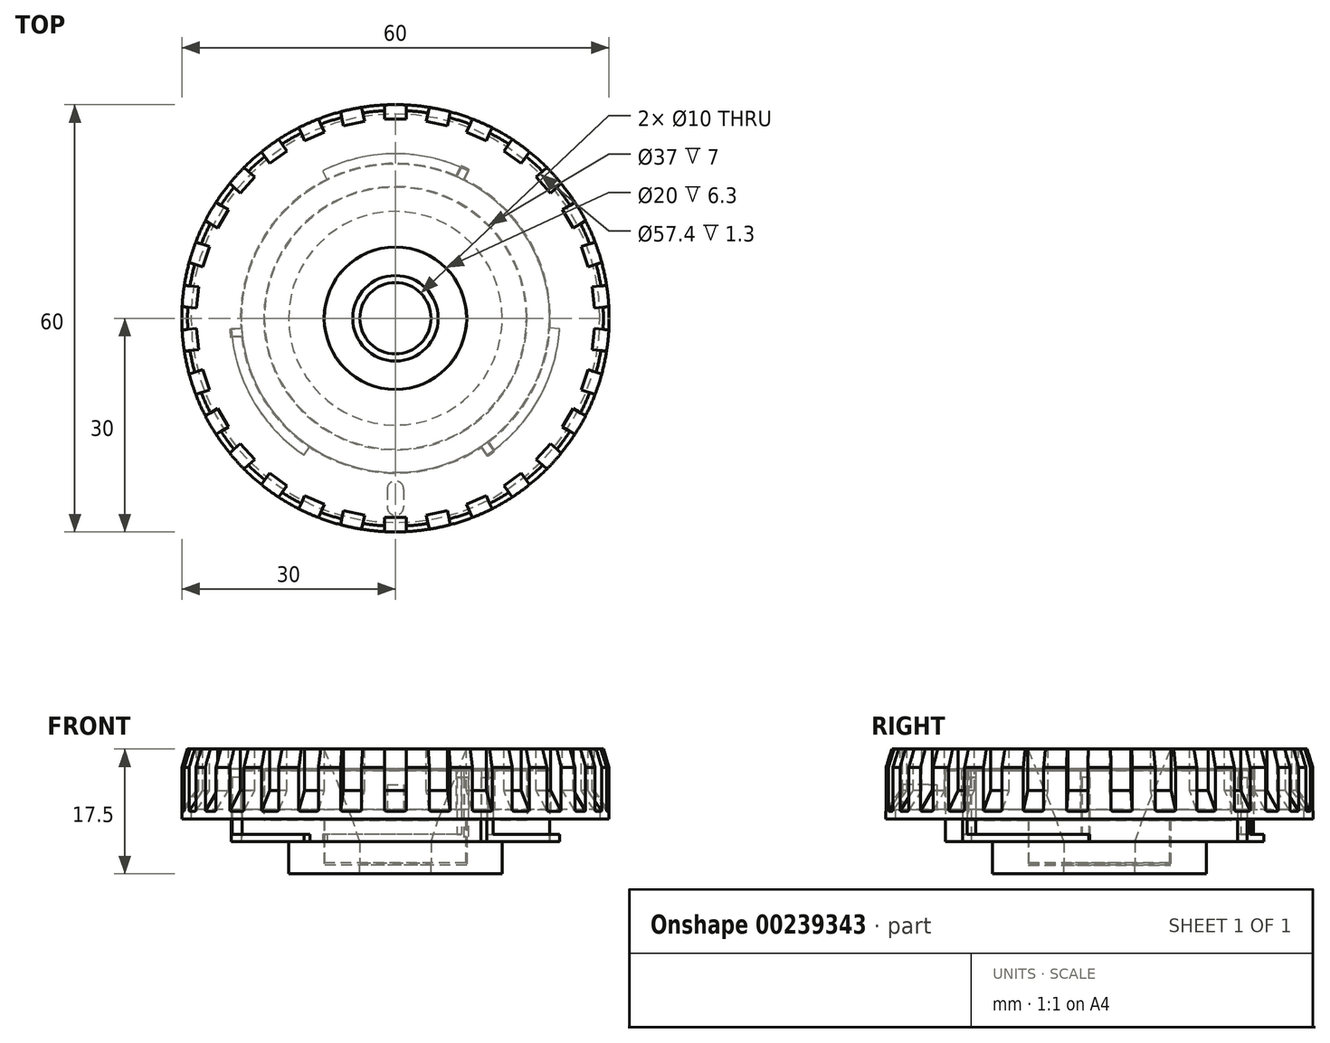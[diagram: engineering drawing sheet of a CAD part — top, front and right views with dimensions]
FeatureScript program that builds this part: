
annotation { "Feature Type Name" : "Feature", "Feature Type Description" : "" }
export const myFeature = defineFeature(function(context is Context, id is Id, definition is map)
    precondition{}
    {
        {
            var Q0;
            Q0=qCreatedBy(makeId("Top.planeOp"),FACE);
            var sketch = newSketch(context, id + "F0", { "sketchPlane" : qUnion([Q0])});
            skCircle(sketch, "E0", {"center": v(0, 0) * mm, "radius": 21.65 * mm});
            skCircle(sketch, "E1", {"center": v(0, 0) * mm, "radius": 18.5 * mm});
            skArc(sketch, "E2", {"start": v(-23.05, -1.47) * mm, "mid": v(-20, -11.55) * mm, "end": v(-12.8, -19.23) * mm});
            skLineSegment(sketch, "E3", {"start": v(0, 0) * mm, "end": v(10.25, 20.7) * mm, "construction": true});
            skLineSegment(sketch, "E4", {"start": v(0, 0) * mm, "end": v(-10.25, 20.7) * mm, "construction": true});
            skLineSegment(sketch, "E5", {"start": v(10.25, 20.7) * mm, "end": v(0, 23.1) * mm, "construction": true});
            skLineSegment(sketch, "E6", {"start": v(0, 23.1) * mm, "end": v(-10.25, 20.7) * mm, "construction": true});
            skLineSegment(sketch, "E7", {"start": v(0, 0) * mm, "end": v(-20, -11.55) * mm, "construction": true});
            skLineSegment(sketch, "E8", {"start": v(0, 0) * mm, "end": v(-23.05, -1.47) * mm, "construction": true});
            skLineSegment(sketch, "E9", {"start": v(0, 0) * mm, "end": v(-12.8, -19.23) * mm, "construction": true});
            skLineSegment(sketch, "E10", {"start": v(0, 0) * mm, "end": v(20, -11.55) * mm, "construction": true});
            skLineSegment(sketch, "E11", {"start": v(0, 0) * mm, "end": v(23.05, -1.47) * mm, "construction": true});
            skLineSegment(sketch, "E12", {"start": v(0, 0) * mm, "end": v(12.8, -19.23) * mm, "construction": true});
            skLineSegment(sketch, "E13", {"start": v(-23.05, -1.47) * mm, "end": v(-12.8, -19.23) * mm, "construction": true});
            skLineSegment(sketch, "E14", {"start": v(23.05, -1.47) * mm, "end": v(12.8, -19.23) * mm, "construction": true});
            skLineSegment(sketch, "E15", {"start": v(-23.05, -1.47) * mm, "end": v(-20, -11.55) * mm, "construction": true});
            skLineSegment(sketch, "E16", {"start": v(-12.8, -19.23) * mm, "end": v(-20, -11.55) * mm, "construction": true});
            skLineSegment(sketch, "E17", {"start": v(12.8, -19.23) * mm, "end": v(20, -11.55) * mm, "construction": true});
            skLineSegment(sketch, "E18", {"start": v(23.05, -1.47) * mm, "end": v(20, -11.55) * mm, "construction": true});
            skLineSegment(sketch, "E19", {"start": v(-10.25, 20.7) * mm, "end": v(-9.6, 19.4) * mm});
            skLineSegment(sketch, "E20", {"start": v(10.25, 20.7) * mm, "end": v(9.6, 19.4) * mm});
            skLineSegment(sketch, "E21", {"start": v(23.05, -1.47) * mm, "end": v(21.6, -1.38) * mm});
            skLineSegment(sketch, "E22", {"start": v(12.8, -19.23) * mm, "end": v(12, -18.02) * mm});
            skLineSegment(sketch, "E23", {"start": v(-23.05, -1.47) * mm, "end": v(-21.6, -1.38) * mm});
            skLineSegment(sketch, "E24", {"start": v(-12.8, -19.23) * mm, "end": v(-12, -18.02) * mm});
            skArc(sketch, "E25.trimOffspring", {"start": v(10.25, 20.7) * mm, "mid": v(0, 23.1) * mm, "end": v(-10.25, 20.7) * mm});
            skArc(sketch, "E26.trimOffspring", {"start": v(12.8, -19.23) * mm, "mid": v(20, -11.55) * mm, "end": v(23.05, -1.47) * mm});
            skCircle(sketch, "E27", {"center": v(0, 0) * mm, "radius": 10 * mm});
            skLineSegment(sketch, "E28", {"start": v(8.6, 19.86) * mm, "end": v(9.25, 21.17) * mm});
            skLineSegment(sketch, "E29", {"start": v(12.9, -17.39) * mm, "end": v(13.7, -18.6) * mm});
            skLineSegment(sketch, "E30", {"start": v(-21.5, -2.48) * mm, "end": v(-22.96, -2.57) * mm});
            skSolve(sketch);
        }
        {
            var Q0;
            Q0=makeQuery(id+"F0.imprint","IMPRINT",FACE,{"disambiguationData":[TD([[makeQuery(id+"F0.imprint","IMPRINT",EDGE,{"derivedFrom":sQuery(id+"F0.wireOp",EDGE,"E1")}),-1.0]])]});
            extrude(context, id + "F1", {"entities" : qUnion([Q0]), "depth" : 10 * mm});
        }
        {
            var Q0;
            Q0=makeQuery(id+"F0.imprint","IMPRINT",FACE,{"disambiguationData":[TD([[makeQuery(id+"F0.imprint","IMPRINT",EDGE,{"derivedFrom":sQuery(id+"F0.wireOp",EDGE,"E1")}),1.0]])]});
            extrude(context, id + "F2", {"entities" : qUnion([Q0]), "operationType" : NewBodyOperationType.ADD, "depth" : 3 * mm});
        }
        {
            var Q0;
            {var subQ0=sQuery(id+"F0.wireOp",EDGE,"E24");Q0=makeQuery(id+"F0.imprint","IMPRINT",FACE,{"disambiguationData":[TD([[makeQuery(id+"F0.imprint","IMPRINT",EDGE,{"derivedFrom":subQ0}),1.0]])]});}
            var Q1;
            {var subQ0=sQuery(id+"F0.wireOp",EDGE,"E21");Q1=makeQuery(id+"F0.imprint","IMPRINT",FACE,{"disambiguationData":[TD([[makeQuery(id+"F0.imprint","IMPRINT",EDGE,{"derivedFrom":subQ0}),1.0]])]});}
            var Q2;
            {var subQ0=sQuery(id+"F0.wireOp",EDGE,"E19");Q2=makeQuery(id+"F0.imprint","IMPRINT",FACE,{"disambiguationData":[TD([[makeQuery(id+"F0.imprint","IMPRINT",EDGE,{"derivedFrom":subQ0}),1.0]])]});}
            extrude(context, id + "F3", {"entities" : qUnion([Q0, Q1, Q2]), "operationType" : NewBodyOperationType.ADD, "depth" : 1 * mm});
        }
        {
            var Q0;
            {var subQ0=sQuery(id+"F0.wireOp",EDGE,"E22");Q0=makeQuery(id+"F0.imprint","IMPRINT",FACE,{"disambiguationData":[TD([[makeQuery(id+"F0.imprint","IMPRINT",EDGE,{"derivedFrom":subQ0}),-1.0]])]});}
            var Q1;
            {var subQ0=sQuery(id+"F0.wireOp",EDGE,"E23");Q1=makeQuery(id+"F0.imprint","IMPRINT",FACE,{"disambiguationData":[TD([[makeQuery(id+"F0.imprint","IMPRINT",EDGE,{"derivedFrom":subQ0}),-1.0]])]});}
            var Q2;
            {var subQ0=sQuery(id+"F0.wireOp",EDGE,"E20");Q2=makeQuery(id+"F0.imprint","IMPRINT",FACE,{"disambiguationData":[TD([[makeQuery(id+"F0.imprint","IMPRINT",EDGE,{"derivedFrom":subQ0}),-1.0]])]});}
            extrude(context, id + "F4", {"entities" : qUnion([Q0, Q1, Q2]), "operationType" : NewBodyOperationType.ADD, "depth" : 9 * mm});
        }
        {
            var Q0;
            Q0=qCreatedBy(makeId("Top.planeOp"),FACE);
            var sketch = newSketch(context, id + "F5", { "sketchPlane" : qUnion([Q0])});
            skCircle(sketch, "E31", {"center": v(0, 0) * mm, "radius": 21.75 * mm});
            skCircle(sketch, "E32", {"center": v(0, 0) * mm, "radius": 18.4 * mm});
            skArc(sketch, "E33", {"start": v(-23.25, -1.53) * mm, "mid": v(-23.2, -2.13) * mm, "end": v(-23.14, -2.72) * mm});
            skLineSegment(sketch, "E34", {"start": v(0, 0) * mm, "end": v(10.3, 20.9) * mm, "construction": true});
            skLineSegment(sketch, "E35", {"start": v(0, 0) * mm, "end": v(-9.61, 19.5) * mm, "construction": true});
            skLineSegment(sketch, "E36", {"start": v(10.3, 20.9) * mm, "end": v(0, 23.3) * mm, "construction": true});
            skLineSegment(sketch, "E37", {"start": v(0, 23.3) * mm, "end": v(-10.3, 20.9) * mm, "construction": true});
            skLineSegment(sketch, "E38", {"start": v(0, 0) * mm, "end": v(-20.18, -11.65) * mm, "construction": true});
            skLineSegment(sketch, "E39", {"start": v(0, 0) * mm, "end": v(-23.25, -1.53) * mm, "construction": true});
            skLineSegment(sketch, "E40", {"start": v(0, 0) * mm, "end": v(-12.09, -18.08) * mm, "construction": true});
            skLineSegment(sketch, "E41", {"start": v(0, 0) * mm, "end": v(20.18, -11.65) * mm, "construction": true});
            skLineSegment(sketch, "E42", {"start": v(0, 0) * mm, "end": v(21.7, -1.43) * mm, "construction": true});
            skLineSegment(sketch, "E43", {"start": v(0, 0) * mm, "end": v(12.95, -19.37) * mm, "construction": true});
            skLineSegment(sketch, "E44", {"start": v(-23.25, -1.53) * mm, "end": v(-12.95, -19.37) * mm, "construction": true});
            skLineSegment(sketch, "E45", {"start": v(23.25, -1.53) * mm, "end": v(12.95, -19.37) * mm, "construction": true});
            skLineSegment(sketch, "E46", {"start": v(-23.25, -1.53) * mm, "end": v(-20.18, -11.65) * mm, "construction": true});
            skLineSegment(sketch, "E47", {"start": v(-12.95, -19.37) * mm, "end": v(-20.18, -11.65) * mm, "construction": true});
            skLineSegment(sketch, "E48", {"start": v(12.95, -19.37) * mm, "end": v(20.18, -11.65) * mm, "construction": true});
            skLineSegment(sketch, "E49", {"start": v(23.25, -1.53) * mm, "end": v(20.18, -11.65) * mm, "construction": true});
            skLineSegment(sketch, "E50", {"start": v(10.3, 20.9) * mm, "end": v(9.61, 19.5) * mm});
            skLineSegment(sketch, "E51", {"start": v(12.95, -19.37) * mm, "end": v(12.09, -18.08) * mm});
            skLineSegment(sketch, "E52", {"start": v(-23.25, -1.53) * mm, "end": v(-21.7, -1.43) * mm});
            skArc(sketch, "E53.trimOffspring", {"start": v(10.3, 20.9) * mm, "mid": v(9.76, 21.16) * mm, "end": v(9.21, 21.4) * mm});
            skArc(sketch, "E54.trimOffspring", {"start": v(12.95, -19.37) * mm, "mid": v(13.44, -19.03) * mm, "end": v(13.93, -18.68) * mm});
            skCircle(sketch, "E55", {"center": v(0, 0) * mm, "radius": 9.9 * mm});
            skLineSegment(sketch, "E56", {"start": v(8.52, 20.01) * mm, "end": v(9.21, 21.4) * mm});
            skLineSegment(sketch, "E57", {"start": v(13.07, -17.39) * mm, "end": v(13.93, -18.68) * mm});
            skLineSegment(sketch, "E58", {"start": v(-21.6, -2.62) * mm, "end": v(-23.14, -2.72) * mm});
            skArc(sketch, "E59.trimOffspring", {"start": v(-20.18, -11.65) * mm, "mid": v(-17, -15.93) * mm, "end": v(-12.95, -19.37) * mm});
            skCircle(sketch, "E60", {"center": v(0, 0) * mm, "radius": 28.7 * mm});
            skCircle(sketch, "E61", {"center": v(0, 0) * mm, "radius": 27.5 * mm});
            skCircle(sketch, "E62", {"center": v(0, 0) * mm, "radius": 26 * mm, "construction": true});
            skArc(sketch, "E63", {"start": v(1.15, -24) * mm, "mid": v(0, -22.85) * mm, "end": v(-1.15, -24) * mm});
            skArc(sketch, "E64", {"start": v(-1.15, -26.5) * mm, "mid": v(0, -27.65) * mm, "end": v(1.15, -26.5) * mm});
            skLineSegment(sketch, "E65", {"start": v(-1.15, -24) * mm, "end": v(-1.15, -26.5) * mm});
            skLineSegment(sketch, "E66", {"start": v(1.15, -24) * mm, "end": v(1.15, -26.5) * mm});
            skCircle(sketch, "E67", {"center": v(0, 0) * mm, "radius": 30 * mm});
            skSolve(sketch);
        }
        {
            var Q0;
            Q0=makeQuery(id+"F5.imprint","IMPRINT",FACE,{"disambiguationData":[TD([[makeQuery(id+"F5.imprint","IMPRINT",EDGE,{"derivedFrom":sQuery(id+"F5.wireOp",EDGE,"E55")}),1.0]])]});
            extrude(context, id + "F6", {"entities" : qUnion([Q0]), "oppositeDirection" : true, "depth" : 3 * mm});
        }
        {
            var Q0;
            Q0=makeQuery(id+"F5.imprint","IMPRINT",FACE,{"disambiguationData":[TD([[makeQuery(id+"F5.imprint","IMPRINT",EDGE,{"derivedFrom":sQuery(id+"F5.wireOp",EDGE,"E55")}),1.0]])]});
            extrude(context, id + "F7", {"entities" : qUnion([Q0]), "operationType" : NewBodyOperationType.ADD, "depth" : 13 * mm});
        }
        {
            var Q0;
            Q0=makeQuery(id+"F5.imprint","IMPRINT",FACE,{"disambiguationData":[TD([[makeQuery(id+"F5.imprint","IMPRINT",EDGE,{"derivedFrom":sQuery(id+"F5.wireOp",EDGE,"E32")}),1.0]])]});
            extrude(context, id + "F8", {"entities" : qUnion([Q0]), "operationType" : NewBodyOperationType.ADD, "depth" : 13 * mm, "hasSecondDirection" : true, "secondDirectionOppositeDirection" : false, "secondDirectionDepth" : 3.2 * mm});
        }
        {
            var Q0;
            Q0=makeQuery(id+"F5.imprint","IMPRINT",FACE,{"disambiguationData":[TD([[makeQuery(id+"F5.imprint","IMPRINT",EDGE,{"derivedFrom":sQuery(id+"F5.wireOp",EDGE,"E32")}),-1.0]])]});
            extrude(context, id + "F9", {"entities" : qUnion([Q0]), "operationType" : NewBodyOperationType.ADD, "depth" : 13 * mm, "hasSecondDirection" : true, "secondDirectionOppositeDirection" : false, "secondDirectionDepth" : 10.2 * mm});
        }
        {
            var Q0;
            Q0=makeQuery(id+"F5.imprint","IMPRINT",FACE,{"disambiguationData":[TD([[makeQuery(id+"F5.imprint","IMPRINT",EDGE,{"derivedFrom":sQuery(id+"F5.wireOp",EDGE,"E33")}),-1.0]])]});
            extrude(context, id + "F10", {"entities" : qUnion([Q0]), "operationType" : NewBodyOperationType.ADD, "depth" : 13 * mm, "hasSecondDirection" : true, "secondDirectionOppositeDirection" : false, "secondDirectionDepth" : 4.5 * mm});
        }
        {
            var Q0;
            {var subQ0=sQuery(id+"F5.wireOp",EDGE,"E51");Q0=makeQuery(id+"F5.imprint","IMPRINT",FACE,{"disambiguationData":[TD([[makeQuery(id+"F5.imprint","IMPRINT",EDGE,{"derivedFrom":subQ0}),-1.0]])]});}
            var Q1;
            Q1=makeQuery(id+"F5.imprint","IMPRINT",FACE,{"disambiguationData":[TD([[makeQuery(id+"F5.imprint","IMPRINT",EDGE,{"derivedFrom":sQuery(id+"F5.wireOp",EDGE,"E33")}),1.0]])]});
            var Q2;
            {var subQ0=sQuery(id+"F5.wireOp",EDGE,"E50");Q2=makeQuery(id+"F5.imprint","IMPRINT",FACE,{"disambiguationData":[TD([[makeQuery(id+"F5.imprint","IMPRINT",EDGE,{"derivedFrom":subQ0}),-1.0]])]});}
            extrude(context, id + "F11", {"entities" : qUnion([Q0, Q1, Q2]), "operationType" : NewBodyOperationType.ADD, "depth" : 13 * mm, "hasSecondDirection" : true, "secondDirectionOppositeDirection" : false, "secondDirectionDepth" : 10.2 * mm});
        }
        {
            var Q0;
            Q0=makeQuery(id+"F5.imprint","IMPRINT",FACE,{"disambiguationData":[TD([[makeQuery(id+"F5.imprint","IMPRINT",EDGE,{"derivedFrom":sQuery(id+"F5.wireOp",EDGE,"E60")}),1.0]])]});
            extrude(context, id + "F12", {"entities" : qUnion([Q0]), "operationType" : NewBodyOperationType.ADD, "depth" : 13 * mm, "hasSecondDirection" : true, "secondDirectionOppositeDirection" : false, "secondDirectionDepth" : 4.5 * mm});
        }
        {
            var Q0;
            Q0=makeQuery(id+"F5.imprint","IMPRINT",FACE,{"disambiguationData":[TD([[makeQuery(id+"F5.imprint","IMPRINT",EDGE,{"derivedFrom":sQuery(id+"F5.wireOp",EDGE,"E60")}),-1.0]])]});
            extrude(context, id + "F13", {"entities" : qUnion([Q0]), "operationType" : NewBodyOperationType.ADD, "depth" : 13 * mm, "hasSecondDirection" : true, "secondDirectionOppositeDirection" : false, "secondDirectionDepth" : 3.2 * mm});
        }
        {
            var Q0;
            Q0=qCreatedBy(makeId("Right.planeOp"),FACE);
            var sketch = newSketch(context, id + "F14", { "sketchPlane" : qUnion([Q0])});
            skLineSegment(sketch, "E68", {"start": v(0, -3) * mm, "end": v(5, -3) * mm});
            skLineSegment(sketch, "E69", {"start": v(6, 3) * mm, "end": v(10, 13) * mm});
            skLineSegment(sketch, "E70", {"start": v(10, 13) * mm, "end": v(0, 13) * mm});
            skLineSegment(sketch, "E71", {"start": v(0, 13) * mm, "end": v(0, -3) * mm});
            skLineSegment(sketch, "E72", {"start": v(5, -3) * mm, "end": v(5, 0) * mm});
            skLineSegment(sketch, "E73", {"start": v(5, 0) * mm, "end": v(6, 3) * mm});
            skLineSegment(sketch, "E74", {"start": v(0, -38) * mm, "end": v(12, -38) * mm, "construction": true});
            skLineSegment(sketch, "E75", {"start": v(0, -38) * mm, "end": v(-12, -38) * mm, "construction": true});
            skLineSegment(sketch, "E76", {"start": v(-12, -38) * mm, "end": v(0, -3) * mm, "construction": true});
            skLineSegment(sketch, "E77", {"start": v(0, -3) * mm, "end": v(16.93, 46.38) * mm, "construction": true});
            skLineSegment(sketch, "E78", {"start": v(0, 28.36) * mm, "end": v(0, -13.33) * mm, "construction": true});
            skSolve(sketch);
        }
        {
            var Q0;
            Q0 = qSketchRegion(id + "F14", true);
            var Q1;
            Q1=sQuery(id+"F14.wireOp",EDGE,"E78");
            revolve(context, id + "F15", {"operationType" : NewBodyOperationType.REMOVE, "entities" : qUnion([Q0]), "axis" : qUnion([Q1]), "revolveType" : RevolveType.FULL, "oppositeDirection" : true});
        }
        {
            var Q0;
            Q0=qCreatedBy(makeId("Right.planeOp"),FACE);
            var sketch = newSketch(context, id + "F16", { "sketchPlane" : qUnion([Q0])});
            skLineSegment(sketch, "E79", {"start": v(-31.45, 13.18) * mm, "end": v(-31.45, 2.18) * mm});
            skLineSegment(sketch, "E80", {"start": v(-31.45, 2.18) * mm, "end": v(-27.95, 7.18) * mm});
            skLineSegment(sketch, "E81", {"start": v(-27.95, 7.18) * mm, "end": v(-27.95, 13.18) * mm});
            skLineSegment(sketch, "E82", {"start": v(-27.95, 13.18) * mm, "end": v(-31.45, 13.18) * mm});
            skLineSegment(sketch, "E83", {"start": v(0, 27.84) * mm, "end": v(0, -20.05) * mm, "construction": true});
            skSolve(sketch);
        }
        {
            var Q0;
            Q0 = qSketchRegion(id + "F16", true);
            extrude(context, id + "F17", {"entities" : qUnion([Q0]), "endBound" : BoundingType.SYMMETRIC, "depth" : 3 * mm});
        }
        {
            var Q0;
            Q0=makeQuery(id+"F17.opExtrude","SWEPT_BODY",BODY,{"disambiguationData":[OSD([sQuery(id+"F16.wireOp",EDGE,"E79"),sQuery(id+"F16.wireOp",EDGE,"E80"),sQuery(id+"F16.wireOp",EDGE,"E81"),sQuery(id+"F16.wireOp",EDGE,"E82")])]});
            var Q1;
            Q1=sQuery(id+"F16.wireOp",EDGE,"E83");
            circularPattern(context, id + "F18", {"operationType" : NewBodyOperationType.REMOVE, "entities" : qUnion([Q0]), "axis" : qUnion([Q1]), "angle" : 360 * degree, "instanceCount" : 30, "equalSpace" : true});
        }
        {
            var Q0;
            Q0=qCreatedBy(makeId("Right.planeOp"),FACE);
            var sketch = newSketch(context, id + "F19", { "sketchPlane" : qUnion([Q0])});
            skLineSegment(sketch, "E84", {"start": v(-30.22, 9.76) * mm, "end": v(-28.86, 14.03) * mm});
            skLineSegment(sketch, "E85", {"start": v(-28.86, 14.03) * mm, "end": v(-30.22, 14.03) * mm});
            skLineSegment(sketch, "E86", {"start": v(-30.22, 14.03) * mm, "end": v(-30.22, 9.76) * mm});
            skSolve(sketch);
        }
        {
            var Q0;
            Q0 = qSketchRegion(id + "F19", true);
            var Q1;
            Q1=sQuery(id+"F16.wireOp",EDGE,"E83");
            revolve(context, id + "F20", {"operationType" : NewBodyOperationType.REMOVE, "entities" : qUnion([Q0]), "axis" : qUnion([Q1]), "revolveType" : RevolveType.FULL, "oppositeDirection" : true});
        }
        {
            var Q0;
            Q0=qCreatedBy(makeId("Top.planeOp"),FACE);
            var sketch = newSketch(context, id + "F21", { "sketchPlane" : qUnion([Q0])});
            skCircle(sketch, "E87", {"center": v(0, 0) * mm, "radius": 10 * mm});
            skCircle(sketch, "E88", {"center": v(0, 0) * mm, "radius": 5 * mm});
            skCircle(sketch, "E89", {"center": v(0, 0) * mm, "radius": 15 * mm});
            skSolve(sketch);
        }
        {
            var Q0;
            Q0=makeQuery(id+"F21.imprint","IMPRINT",FACE,{"disambiguationData":[TD([[makeQuery(id+"F21.imprint","IMPRINT",EDGE,{"derivedFrom":sQuery(id+"F21.wireOp",EDGE,"E87")}),1.0]])]});
            extrude(context, id + "F22", {"entities" : qUnion([Q0]), "oppositeDirection" : true, "depth" : 4.5 * mm, "hasSecondDirection" : true, "secondDirectionOppositeDirection" : true, "secondDirectionDepth" : 3.3 * mm});
        }
        {
            var Q0;
            Q0=makeQuery(id+"F21.imprint","IMPRINT",FACE,{"disambiguationData":[TD([[makeQuery(id+"F21.imprint","IMPRINT",EDGE,{"derivedFrom":sQuery(id+"F21.wireOp",EDGE,"E87")}),-1.0]])]});
            extrude(context, id + "F23", {"entities" : qUnion([Q0]), "operationType" : NewBodyOperationType.ADD, "oppositeDirection" : true, "depth" : 4.5 * mm, "hasSecondDirection" : true, "secondDirectionOppositeDirection" : false, "secondDirectionDepth" : 0.1 * mm});
        }
        {
            var Q0;
            Q0=makeQuery(id+"F5.imprint","IMPRINT",FACE,{"disambiguationData":[TD([[makeQuery(id+"F5.imprint","IMPRINT",EDGE,{"derivedFrom":sQuery(id+"F5.wireOp",EDGE,"E63")}),1.0]])]});
            var Q1;
            {var subQ0=sQuery(id+"F5.wireOp",EDGE,"E64");var subQ1=sQuery(id+"F5.wireOp",EDGE,"E61");var subQ2=makeQuery(id+"F5.imprint","INTERSECT",VERTEX,{"disambiguationData":[OD(0.0)],"derivedFrom":[subQ1,subQ0]});Q1=makeQuery(id+"F5.imprint","IMPRINT",FACE,{"disambiguationData":[TD([[makeQuery(id+"F5.imprint","IMPRINT",EDGE,{"disambiguationData":[TD([[subQ2,-1.0]])],"derivedFrom":subQ1}),-1.0]])]});}
            extrude(context, id + "F24", {"entities" : qUnion([Q0, Q1]), "operationType" : NewBodyOperationType.ADD, "depth" : 13 * mm, "hasSecondDirection" : true, "secondDirectionOppositeDirection" : false, "secondDirectionDepth" : 8 * mm});
        }
    });
